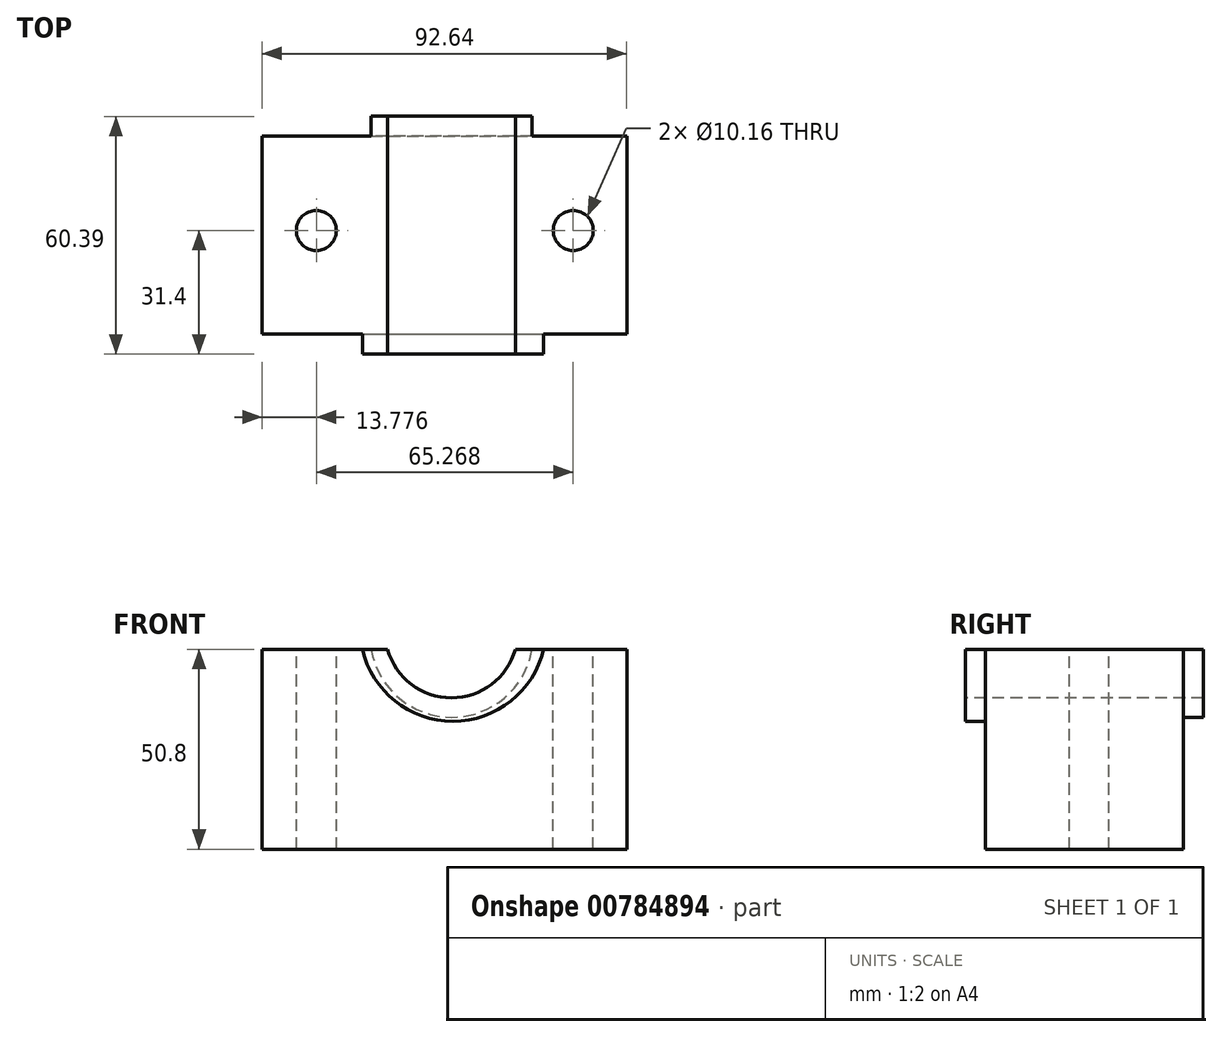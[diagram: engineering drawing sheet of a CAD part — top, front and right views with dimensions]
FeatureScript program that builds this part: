
annotation { "Feature Type Name" : "Feature", "Feature Type Description" : "" }
export const myFeature = defineFeature(function(context is Context, id is Id, definition is map)
    precondition{}
    {
        {
            var Q0;
            Q0=qCreatedBy(makeId("Top.planeOp"),FACE);
            var sketch = newSketch(context, id + "F0", { "sketchPlane" : qUnion([Q0])});
            skLineSegment(sketch, "E0.bottom", {"start": v(-45.87, 23.91) * mm, "end": v(46.77, 23.91) * mm});
            skLineSegment(sketch, "E0.top", {"start": v(-45.87, -26.32) * mm, "end": v(46.77, -26.32) * mm});
            skLineSegment(sketch, "E0.left", {"start": v(-45.87, 23.91) * mm, "end": v(-45.87, -26.32) * mm});
            skLineSegment(sketch, "E0.right", {"start": v(46.77, 23.91) * mm, "end": v(46.77, -26.32) * mm});
            skSolve(sketch);
        }
        {
            var Q0;
            Q0 = qSketchRegion(id + "F0", true);
            extrude(context, id + "F1", {"entities" : qUnion([Q0]), "depth" : 50.8 * mm, "offsetDistance" : 25.4 * mm});
        }
        {
            var Q0;
            Q0=makeQuery(id+"F1.opExtrude","SWEPT_FACE",FACE,{"disambiguationData":[OSD([sQuery(id+"F0.wireOp",EDGE,"E0.top")])]});
            var sketch = newSketch(context, id + "F2", { "sketchPlane" : qUnion([Q0])});
            skArc(sketch, "E1", {"start": v(-13.98, 50.8) * mm, "mid": v(2.24, 38.44) * mm, "end": v(18.46, 50.8) * mm});
            skArc(sketch, "E2", {"start": v(-20.4, 50.8) * mm, "mid": v(2.62, 32.47) * mm, "end": v(25.64, 50.8) * mm});
            skSolve(sketch);
        }
        {
            var Q0;
            {var subQ0=sQuery(id+"F2.wireOp",EDGE,"E1");Q0=makeQuery(id+"F2.imprint","IMPRINT",FACE,{"disambiguationData":[TD([[makeQuery(id+"F2.imprint","IMPRINT",EDGE,{"derivedFrom":subQ0}),1.0]])]});}
            extrude(context, id + "F3", {"entities" : qUnion([Q0]), "operationType" : NewBodyOperationType.REMOVE, "oppositeDirection" : true, "depth" : 91.95 * mm, "offsetDistance" : 25.4 * mm});
        }
        {
            var Q0;
            {var subQ0=sQuery(id+"F2.wireOp",EDGE,"E1");Q0=makeQuery(id+"F2.imprint","IMPRINT",FACE,{"disambiguationData":[TD([[makeQuery(id+"F2.imprint","IMPRINT",EDGE,{"derivedFrom":subQ0}),-1.0]])]});}
            extrude(context, id + "F4", {"entities" : qUnion([Q0]), "operationType" : NewBodyOperationType.ADD, "depth" : 5.08 * mm, "offsetDistance" : 25.4 * mm});
        }
        {
            var Q0;
            Q0=makeQuery(id+"F1.opExtrude","SWEPT_FACE",FACE,{"disambiguationData":[OSD([sQuery(id+"F0.wireOp",EDGE,"E0.bottom")])]});
            var sketch = newSketch(context, id + "F5", { "sketchPlane" : qUnion([Q0])});
            skArc(sketch, "E3", {"start": v(-22.76, 50.8) * mm, "mid": v(-2.3, 33.52) * mm, "end": v(18.18, 50.8) * mm});
            skSolve(sketch);
        }
        {
            var Q0;
            {var subQ0=sQuery(id+"F5.wireOp",EDGE,"E3");Q0=makeQuery(id+"F5.imprint","IMPRINT",FACE,{"disambiguationData":[TD([[makeQuery(id+"F5.imprint","IMPRINT",EDGE,{"derivedFrom":subQ0}),1.0]])]});}
            extrude(context, id + "F6", {"entities" : qUnion([Q0]), "operationType" : NewBodyOperationType.ADD, "depth" : 5.08 * mm, "offsetDistance" : 25.4 * mm});
        }
        {
            var Q0;
            {var subQ0=sQuery(id+"F0.wireOp",EDGE,"E0.bottom");var subQ2=sQuery(id+"F0.wireOp",EDGE,"E0.left");var subQ3=sQuery(id+"F0.wireOp",EDGE,"E0.top");var subQ4=makeQuery(id+"F1.opExtrude","CAP_FACE",FACE,{"disambiguationData":[OSD([subQ0,subQ3,subQ2,sQuery(id+"F0.wireOp",EDGE,"E0.right")])],"isStart":false});var subQ5=makeQuery(id+"F1.opExtrude","SWEPT_FACE",FACE,{"disambiguationData":[OSD([subQ2])]});var subQ6=sQuery(id+"F2.wireOp",EDGE,"E1");var subQ8=makeQuery(id+"F3.boolean.opBoolean","SPLIT",EDGE,{"disambiguationData":[TD([subQ5])],"derivedFrom":makeQuery(id+"F1.opExtrude","CAP_EDGE",EDGE,{"disambiguationData":[OSD([subQ0])],"isStart":false})});var subQ9=makeQuery(id+"F1.opExtrude","CAP_EDGE",EDGE,{"disambiguationData":[OSD([subQ3])],"isStart":false});Q0=makeQuery(id+"F6.boolean.opBoolean","MERGE",FACE,{"derivedFrom":[makeQuery(id+"F4.boolean.opBoolean","MERGE",FACE,{"derivedFrom":[makeQuery(id+"F3.boolean.opBoolean","SPLIT",FACE,{"disambiguationData":[TD([subQ5])],"derivedFrom":subQ4}),makeQuery(id+"F4.opExtrude","SWEPT_FACE",FACE,{"disambiguationData":[OSD([subQ3]),TDD([makeQuery(id+"F2.imprint","IMPRINT",EDGE,{"disambiguationData":[TD([[makeQuery(id+"F2.imprint","INTERSECT",VERTEX,{"disambiguationData":[OD(0.0)],"derivedFrom":[subQ9,subQ6]}),1.0]])],"derivedFrom":subQ9})])]})]}),makeQuery(id+"F6.opExtrude","SWEPT_FACE",FACE,{"disambiguationData":[OSD([subQ0]),TDD([makeQuery(id+"F5.imprint","IMPRINT",EDGE,{"disambiguationData":[TD([[makeQuery(id+"F5.imprint","INTERSECT",VERTEX,{"derivedFrom":[subQ8,sQuery(id+"F5.wireOp",EDGE,"E3")]}),-1.0]])],"derivedFrom":subQ8})])]})]});}
            var sketch = newSketch(context, id + "F7", { "sketchPlane" : qUnion([Q0])});
            skCircle(sketch, "E4", {"center": v(-32.1, 0) * mm, "radius": 5.28 * mm});
            skSolve(sketch);
        }
        {
            var Q0;
            {var subQ0=sQuery(id+"F0.wireOp",EDGE,"E0.bottom");var subQ2=sQuery(id+"F0.wireOp",EDGE,"E0.right");var subQ3=makeQuery(id+"F1.opExtrude","SWEPT_FACE",FACE,{"disambiguationData":[OSD([subQ2])]});var subQ4=sQuery(id+"F0.wireOp",EDGE,"E0.top");var subQ5=makeQuery(id+"F1.opExtrude","CAP_FACE",FACE,{"disambiguationData":[OSD([subQ0,subQ4,sQuery(id+"F0.wireOp",EDGE,"E0.left"),subQ2])],"isStart":false});var subQ6=sQuery(id+"F2.wireOp",EDGE,"E1");var subQ8=makeQuery(id+"F3.boolean.opBoolean","SPLIT",EDGE,{"disambiguationData":[TD([subQ3])],"derivedFrom":makeQuery(id+"F1.opExtrude","CAP_EDGE",EDGE,{"disambiguationData":[OSD([subQ0])],"isStart":false})});var subQ9=makeQuery(id+"F1.opExtrude","CAP_EDGE",EDGE,{"disambiguationData":[OSD([subQ4])],"isStart":false});Q0=makeQuery(id+"F6.boolean.opBoolean","MERGE",FACE,{"derivedFrom":[makeQuery(id+"F4.boolean.opBoolean","MERGE",FACE,{"derivedFrom":[makeQuery(id+"F3.boolean.opBoolean","SPLIT",FACE,{"disambiguationData":[TD([subQ3])],"derivedFrom":subQ5}),makeQuery(id+"F4.opExtrude","SWEPT_FACE",FACE,{"disambiguationData":[OSD([subQ4]),TDD([makeQuery(id+"F2.imprint","IMPRINT",EDGE,{"disambiguationData":[TD([[makeQuery(id+"F2.imprint","INTERSECT",VERTEX,{"disambiguationData":[OD(1.0)],"derivedFrom":[subQ9,subQ6]}),-1.0]])],"derivedFrom":subQ9})])]})]}),makeQuery(id+"F6.opExtrude","SWEPT_FACE",FACE,{"disambiguationData":[OSD([subQ0]),TDD([makeQuery(id+"F5.imprint","IMPRINT",EDGE,{"disambiguationData":[TD([[makeQuery(id+"F5.imprint","INTERSECT",VERTEX,{"derivedFrom":[subQ8,sQuery(id+"F5.wireOp",EDGE,"E3")]}),1.0]])],"derivedFrom":subQ8})])]})]});}
            var sketch = newSketch(context, id + "F8", { "sketchPlane" : qUnion([Q0])});
            skCircle(sketch, "E5", {"center": v(33.17, 0) * mm, "radius": 5.28 * mm});
            skSolve(sketch);
        }
        {
            var Q0;
            Q0=sQuery(id+"F7.wireOp",VERTEX,"E4.center");
            var Q1;
            Q1=sQuery(id+"F8.wireOp",VERTEX,"E5.center");
            var Q2;
            Q2=makeQuery(id+"F1.opExtrude","SWEPT_BODY",BODY,{"disambiguationData":[OSD([sQuery(id+"F0.wireOp",EDGE,"E0.bottom"),sQuery(id+"F0.wireOp",EDGE,"E0.top"),sQuery(id+"F0.wireOp",EDGE,"E0.left"),sQuery(id+"F0.wireOp",EDGE,"E0.right")])]});
            hole(context, id + "F9", {"style" : HoleStyle.SIMPLE, "endStyle" : HoleEndStyle.THROUGH, "holeDiameter" : 10.16 * mm, "majorDiameter" : 6.35 * mm, "isTappedThrough" : true, "tappedDepth" : 12.7 * mm, "tapClearance" : 3, "locations" : qUnion([Q0, Q1]), "scope" : qUnion([Q2])});
        }
    });
